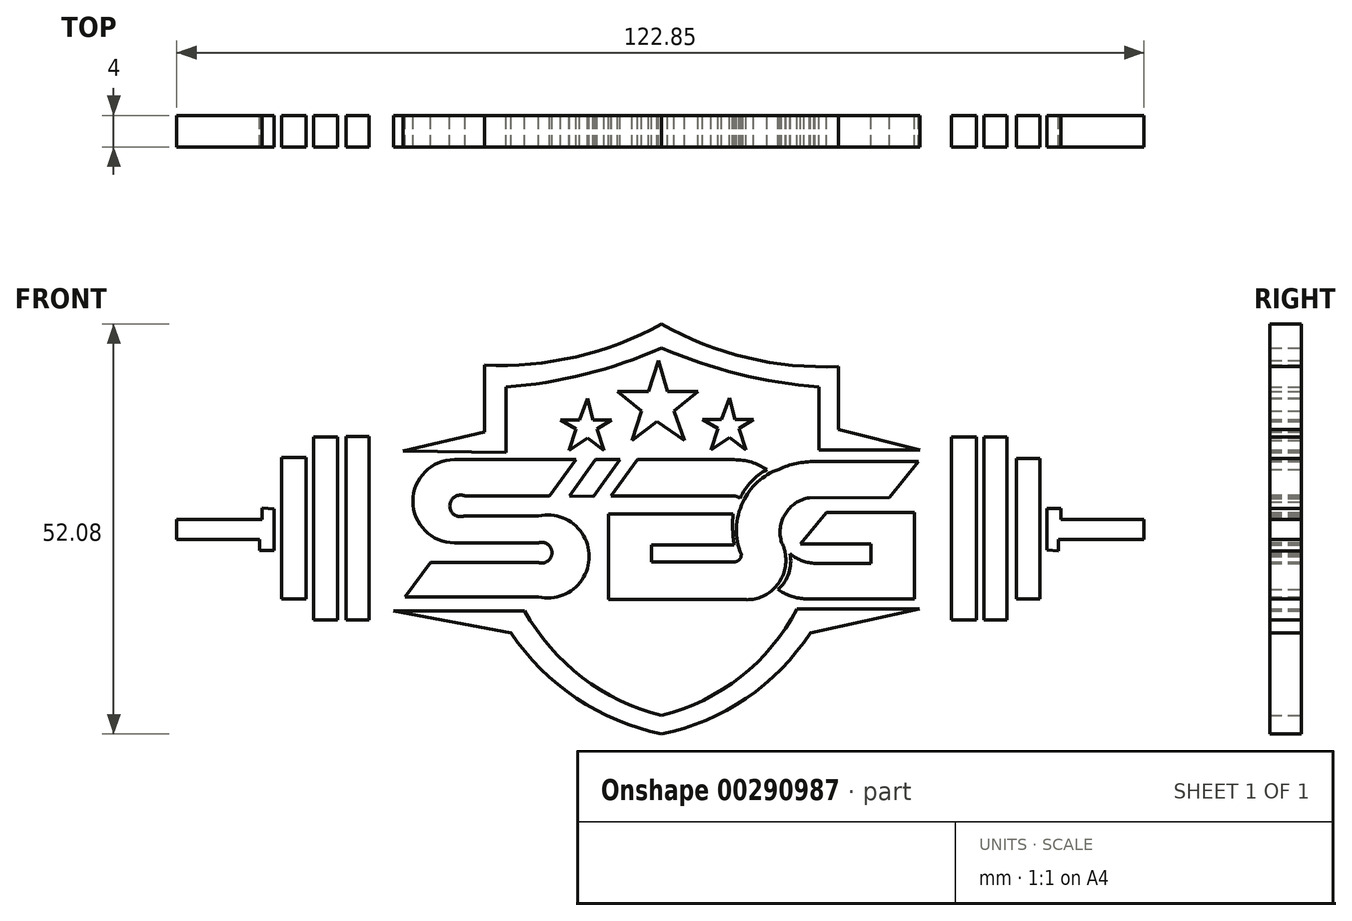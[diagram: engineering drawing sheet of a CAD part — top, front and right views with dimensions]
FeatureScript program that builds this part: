
annotation { "Feature Type Name" : "Feature", "Feature Type Description" : "" }
export const myFeature = defineFeature(function(context is Context, id is Id, definition is map)
    precondition{}
    {
        {
            var Q0;
            Q0=qCreatedBy(makeId("Front.planeOp"),FACE);
            var sketch = newSketch(context, id + "F0", { "sketchPlane" : qUnion([Q0])});
            skLineSegment(sketch, "E0", {"start": v(-28.73, 27.46) * mm, "end": v(-18.36, 29.84) * mm});
            skLineSegment(sketch, "E1", {"start": v(-18.36, 29.84) * mm, "end": v(-18.36, 38.37) * mm});
            skLineSegment(sketch, "E2", {"start": v(26.58, 38.16) * mm, "end": v(26.58, 30.16) * mm});
            skLineSegment(sketch, "E3", {"start": v(26.58, 30.16) * mm, "end": v(36.96, 27.57) * mm});
            skLineSegment(sketch, "E4", {"start": v(36.96, 27.57) * mm, "end": v(24.1, 27.57) * mm});
            skLineSegment(sketch, "E5", {"start": v(24.1, 27.57) * mm, "end": v(24.1, 35.56) * mm});
            skLineSegment(sketch, "E6", {"start": v(-15.66, 35.56) * mm, "end": v(-15.66, 27.24) * mm});
            skLineSegment(sketch, "E7", {"start": v(-15.66, 27.24) * mm, "end": v(-28.73, 27.46) * mm});
            skArc(sketch, "E8", {"start": v(-18.36, 38.37) * mm, "mid": v(-6.76, 39.4) * mm, "end": v(4.11, 43.56) * mm});
            skArc(sketch, "E9", {"start": v(4.11, 43.56) * mm, "mid": v(14.97, 39.29) * mm, "end": v(26.58, 38.16) * mm});
            skArc(sketch, "E10", {"start": v(-15.66, 35.56) * mm, "mid": v(-5.56, 37.2) * mm, "end": v(4.11, 40.53) * mm});
            skArc(sketch, "E11", {"start": v(4.11, 40.53) * mm, "mid": v(13.9, 37.21) * mm, "end": v(24.1, 35.56) * mm});
            skLineSegment(sketch, "E12", {"start": v(-29.92, 7.15) * mm, "end": v(-13.28, 7.15) * mm});
            skLineSegment(sketch, "E13", {"start": v(21.29, 7.37) * mm, "end": v(36.85, 7.37) * mm});
            skLineSegment(sketch, "E14", {"start": v(36.85, 7.37) * mm, "end": v(23.02, 4.34) * mm});
            skLineSegment(sketch, "E15", {"start": v(-15.01, 4.34) * mm, "end": v(-29.92, 7.15) * mm});
            skArc(sketch, "E16", {"start": v(-13.28, 7.15) * mm, "mid": v(-5.98, -1.32) * mm, "end": v(4.11, -6.14) * mm});
            skArc(sketch, "E17", {"start": v(4.11, -6.14) * mm, "mid": v(14.17, -1.26) * mm, "end": v(21.29, 7.37) * mm});
            skArc(sketch, "E18", {"start": v(4.11, -8.52) * mm, "mid": v(14.86, -4) * mm, "end": v(23.02, 4.34) * mm});
            skArc(sketch, "E19", {"start": v(-15.01, 4.34) * mm, "mid": v(-6.71, -3.97) * mm, "end": v(4.11, -8.52) * mm});
            skLineSegment(sketch, "E20.bottom", {"start": v(-35.97, 29.3) * mm, "end": v(-33.05, 29.3) * mm});
            skLineSegment(sketch, "E20.top", {"start": v(-35.97, 5.96) * mm, "end": v(-33.05, 5.96) * mm});
            skLineSegment(sketch, "E20.left", {"start": v(-35.97, 29.3) * mm, "end": v(-35.97, 5.96) * mm});
            skLineSegment(sketch, "E20.right", {"start": v(-33.05, 29.3) * mm, "end": v(-33.05, 5.96) * mm});
            skLineSegment(sketch, "E21.bottom", {"start": v(-40.08, 29.19) * mm, "end": v(-37.05, 29.19) * mm});
            skLineSegment(sketch, "E21.top", {"start": v(-40.08, 5.96) * mm, "end": v(-37.05, 5.96) * mm});
            skLineSegment(sketch, "E21.left", {"start": v(-40.08, 29.19) * mm, "end": v(-40.08, 5.96) * mm});
            skLineSegment(sketch, "E21.right", {"start": v(-37.05, 29.19) * mm, "end": v(-37.05, 5.96) * mm});
            skLineSegment(sketch, "E22.bottom", {"start": v(-44.18, 26.6) * mm, "end": v(-41.05, 26.6) * mm});
            skLineSegment(sketch, "E22.top", {"start": v(-44.18, 8.66) * mm, "end": v(-41.05, 8.66) * mm});
            skLineSegment(sketch, "E22.left", {"start": v(-44.18, 26.6) * mm, "end": v(-44.18, 8.66) * mm});
            skLineSegment(sketch, "E22.right", {"start": v(-41.05, 26.6) * mm, "end": v(-41.05, 8.66) * mm});
            skLineSegment(sketch, "E23.bottom", {"start": v(40.95, 29.19) * mm, "end": v(44.09, 29.19) * mm});
            skLineSegment(sketch, "E23.top", {"start": v(40.95, 5.96) * mm, "end": v(44.09, 5.96) * mm});
            skLineSegment(sketch, "E23.left", {"start": v(40.95, 29.19) * mm, "end": v(40.95, 5.96) * mm});
            skLineSegment(sketch, "E23.right", {"start": v(44.09, 29.19) * mm, "end": v(44.09, 5.96) * mm});
            skLineSegment(sketch, "E24.bottom", {"start": v(45.06, 29.19) * mm, "end": v(47.98, 29.19) * mm});
            skLineSegment(sketch, "E24.top", {"start": v(45.06, 5.96) * mm, "end": v(47.98, 5.96) * mm});
            skLineSegment(sketch, "E24.left", {"start": v(45.06, 29.19) * mm, "end": v(45.06, 5.96) * mm});
            skLineSegment(sketch, "E24.right", {"start": v(47.98, 29.19) * mm, "end": v(47.98, 5.96) * mm});
            skLineSegment(sketch, "E25.bottom", {"start": v(49.16, 26.49) * mm, "end": v(52.19, 26.49) * mm});
            skLineSegment(sketch, "E25.top", {"start": v(49.16, 8.66) * mm, "end": v(52.19, 8.66) * mm});
            skLineSegment(sketch, "E25.left", {"start": v(49.16, 26.49) * mm, "end": v(49.16, 8.66) * mm});
            skLineSegment(sketch, "E25.right", {"start": v(52.19, 26.49) * mm, "end": v(52.19, 8.66) * mm});
            skLineSegment(sketch, "E26", {"start": v(-45.11, 20.09) * mm, "end": v(-45.11, 14.82) * mm});
            skLineSegment(sketch, "E27", {"start": v(-45.11, 14.82) * mm, "end": v(-46.94, 14.82) * mm});
            skLineSegment(sketch, "E28", {"start": v(-46.94, 14.82) * mm, "end": v(-46.94, 16.2) * mm});
            skLineSegment(sketch, "E29", {"start": v(-46.94, 16.2) * mm, "end": v(-57.46, 16.2) * mm});
            skLineSegment(sketch, "E30", {"start": v(-57.46, 16.2) * mm, "end": v(-57.46, 18.72) * mm});
            skLineSegment(sketch, "E31", {"start": v(-57.46, 18.72) * mm, "end": v(-46.6, 18.72) * mm});
            skLineSegment(sketch, "E32", {"start": v(-46.6, 18.72) * mm, "end": v(-46.6, 20.2) * mm});
            skLineSegment(sketch, "E33", {"start": v(-46.6, 20.2) * mm, "end": v(-45.11, 20.09) * mm});
            skLineSegment(sketch, "E34", {"start": v(53.04, 14.85) * mm, "end": v(53.04, 20.12) * mm});
            skLineSegment(sketch, "E35", {"start": v(53.04, 20.12) * mm, "end": v(54.87, 20.12) * mm});
            skLineSegment(sketch, "E36", {"start": v(54.87, 20.12) * mm, "end": v(54.87, 18.74) * mm});
            skLineSegment(sketch, "E37", {"start": v(54.87, 18.74) * mm, "end": v(65.39, 18.74) * mm});
            skLineSegment(sketch, "E38", {"start": v(65.39, 18.74) * mm, "end": v(65.39, 16.22) * mm});
            skLineSegment(sketch, "E39", {"start": v(65.39, 16.22) * mm, "end": v(54.53, 16.22) * mm});
            skLineSegment(sketch, "E40", {"start": v(54.53, 16.22) * mm, "end": v(54.53, 14.74) * mm});
            skLineSegment(sketch, "E41", {"start": v(54.53, 14.74) * mm, "end": v(53.04, 14.85) * mm});
            skLineSegment(sketch, "E42", {"start": v(-8.71, 31.4) * mm, "end": v(-6.3, 31.4) * mm});
            skPoint(sketch, "E42.startSnap0", {"position": v(-15.66, 31.4) * mm});
            skLineSegment(sketch, "E43", {"start": v(-6.3, 31.4) * mm, "end": v(-5.28, 34.1) * mm});
            skLineSegment(sketch, "E44", {"start": v(-5.28, 34.1) * mm, "end": v(-4.56, 31.4) * mm});
            skLineSegment(sketch, "E45", {"start": v(-4.56, 31.4) * mm, "end": v(-2.22, 31.4) * mm});
            skLineSegment(sketch, "E46", {"start": v(-2.22, 31.4) * mm, "end": v(-4.06, 30.22) * mm});
            skLineSegment(sketch, "E47", {"start": v(-4.06, 30.22) * mm, "end": v(-3.2, 27.48) * mm});
            skLineSegment(sketch, "E48", {"start": v(-3.2, 27.48) * mm, "end": v(-5.28, 29.07) * mm});
            skLineSegment(sketch, "E49", {"start": v(-5.28, 29.07) * mm, "end": v(-7.63, 27.48) * mm});
            skLineSegment(sketch, "E50", {"start": v(-7.63, 27.48) * mm, "end": v(-6.76, 30.22) * mm});
            skLineSegment(sketch, "E51", {"start": v(-6.76, 30.22) * mm, "end": v(-8.71, 31.4) * mm});
            skLineSegment(sketch, "E52", {"start": v(3.55, 31.2) * mm, "end": v(0.34, 28.75) * mm});
            skLineSegment(sketch, "E53", {"start": v(0.34, 28.75) * mm, "end": v(1.57, 32.53) * mm});
            skLineSegment(sketch, "E54", {"start": v(1.57, 32.53) * mm, "end": v(-1.5, 34.99) * mm});
            skLineSegment(sketch, "E55", {"start": v(-1.5, 34.99) * mm, "end": v(2.47, 34.99) * mm});
            skLineSegment(sketch, "E56", {"start": v(2.47, 34.99) * mm, "end": v(3.75, 38.94) * mm});
            skLineSegment(sketch, "E57", {"start": v(3.75, 38.94) * mm, "end": v(4.85, 34.99) * mm});
            skLineSegment(sketch, "E58", {"start": v(4.85, 34.99) * mm, "end": v(8.75, 34.99) * mm});
            skLineSegment(sketch, "E59", {"start": v(8.75, 34.99) * mm, "end": v(5.72, 32.53) * mm});
            skLineSegment(sketch, "E60", {"start": v(5.72, 32.53) * mm, "end": v(7.02, 28.78) * mm});
            skLineSegment(sketch, "E61", {"start": v(7.02, 28.78) * mm, "end": v(3.55, 31.2) * mm});
            skLineSegment(sketch, "E62", {"start": v(9.32, 31.47) * mm, "end": v(11.72, 31.47) * mm});
            skLineSegment(sketch, "E63", {"start": v(11.72, 31.47) * mm, "end": v(12.75, 34.16) * mm});
            skLineSegment(sketch, "E64", {"start": v(12.75, 34.16) * mm, "end": v(13.46, 31.47) * mm});
            skLineSegment(sketch, "E65", {"start": v(13.46, 31.47) * mm, "end": v(15.8, 31.47) * mm});
            skLineSegment(sketch, "E66", {"start": v(15.8, 31.47) * mm, "end": v(13.97, 30.29) * mm});
            skLineSegment(sketch, "E67", {"start": v(13.97, 30.29) * mm, "end": v(14.83, 27.55) * mm});
            skLineSegment(sketch, "E68", {"start": v(14.83, 27.55) * mm, "end": v(12.75, 29.13) * mm});
            skLineSegment(sketch, "E69", {"start": v(12.75, 29.13) * mm, "end": v(10.4, 27.55) * mm});
            skLineSegment(sketch, "E70", {"start": v(10.4, 27.55) * mm, "end": v(11.27, 30.29) * mm});
            skLineSegment(sketch, "E71", {"start": v(11.27, 30.29) * mm, "end": v(9.32, 31.47) * mm});
            skLineSegment(sketch, "E72", {"start": v(-6.76, 26.33) * mm, "end": v(-22.2, 26.33) * mm});
            skPoint(sketch, "E72.endSnap0", {"position": v(-22.2, 27.35) * mm});
            skArc(sketch, "E73", {"start": v(-22.2, 26.33) * mm, "mid": v(-27.47, 21.05) * mm, "end": v(-22.2, 15.78) * mm});
            skLineSegment(sketch, "E74", {"start": v(-22.2, 15.78) * mm, "end": v(-11.5, 15.78) * mm});
            skLineSegment(sketch, "E75", {"start": v(-11.5, 13.26) * mm, "end": v(-25.22, 13.26) * mm});
            skLineSegment(sketch, "E76", {"start": v(-25.22, 13.26) * mm, "end": v(-28.48, 8.87) * mm});
            skLineSegment(sketch, "E77", {"start": v(-28.48, 8.87) * mm, "end": v(-11.5, 8.87) * mm});
            skLineSegment(sketch, "E78", {"start": v(-11.5, 19.2) * mm, "end": v(-20.87, 19.2) * mm});
            skLineSegment(sketch, "E79", {"start": v(-20.87, 21.72) * mm, "end": v(-10.1, 21.72) * mm});
            skLineSegment(sketch, "E80", {"start": v(-10.1, 21.72) * mm, "end": v(-6.76, 26.33) * mm});
            skArc(sketch, "E81", {"start": v(-20.87, 21.72) * mm, "mid": v(-22.78, 20.46) * mm, "end": v(-20.87, 19.2) * mm});
            skArc(sketch, "E82", {"start": v(-11.5, 13.26) * mm, "mid": v(-9.8, 14.52) * mm, "end": v(-11.5, 15.78) * mm});
            skArc(sketch, "E83", {"start": v(-11.5, 8.87) * mm, "mid": v(-5.1, 14.04) * mm, "end": v(-11.5, 19.2) * mm});
            skLineSegment(sketch, "E84", {"start": v(-4.24, 26.33) * mm, "end": v(-7.59, 21.72) * mm});
            skLineSegment(sketch, "E85", {"start": v(-7.59, 21.72) * mm, "end": v(-4.52, 21.67) * mm});
            skLineSegment(sketch, "E86", {"start": v(-4.52, 21.67) * mm, "end": v(-1.14, 26.33) * mm});
            skLineSegment(sketch, "E87", {"start": v(-1.14, 26.33) * mm, "end": v(-4.24, 26.33) * mm});
            skLineSegment(sketch, "E88", {"start": v(1.04, 26.33) * mm, "end": v(-2.3, 21.72) * mm});
            skLineSegment(sketch, "E89", {"start": v(-2.3, 21.72) * mm, "end": v(13.27, 21.72) * mm});
            skLineSegment(sketch, "E90", {"start": v(13.34, 26.33) * mm, "end": v(1.04, 26.33) * mm});
            skArc(sketch, "E91", {"start": v(17.5, 25.08) * mm, "mid": v(15.5, 26) * mm, "end": v(13.34, 26.33) * mm});
            skArc(sketch, "E92", {"start": v(17.5, 25.08) * mm, "mid": v(15.5, 23.52) * mm, "end": v(14.07, 21.43) * mm});
            skArc(sketch, "E93", {"start": v(14.07, 21.43) * mm, "mid": v(13.7, 21.65) * mm, "end": v(13.27, 21.72) * mm});
            skLineSegment(sketch, "E94", {"start": v(13.2, 19.4) * mm, "end": v(-2.62, 19.42) * mm});
            skLineSegment(sketch, "E95", {"start": v(-2.62, 19.42) * mm, "end": v(-2.62, 8.55) * mm});
            skLineSegment(sketch, "E96", {"start": v(-2.62, 8.55) * mm, "end": v(14.93, 8.55) * mm});
            skArc(sketch, "E97", {"start": v(14.93, 8.55) * mm, "mid": v(18.63, 10.2) * mm, "end": v(19.88, 14.06) * mm});
            skArc(sketch, "E98", {"start": v(19.88, 14.06) * mm, "mid": v(19.71, 14.96) * mm, "end": v(19.37, 15.8) * mm});
            skArc(sketch, "E99", {"start": v(22.88, 21.5) * mm, "mid": v(19.83, 19.45) * mm, "end": v(19.37, 15.8) * mm});
            skArc(sketch, "E100", {"start": v(13.2, 19.4) * mm, "mid": v(13.15, 17.46) * mm, "end": v(13.34, 15.52) * mm});
            skLineSegment(sketch, "E101", {"start": v(13.34, 15.52) * mm, "end": v(2.81, 15.53) * mm});
            skLineSegment(sketch, "E102", {"start": v(2.81, 15.53) * mm, "end": v(2.81, 13.36) * mm});
            skLineSegment(sketch, "E103", {"start": v(2.81, 13.36) * mm, "end": v(13.34, 13.35) * mm});
            skArc(sketch, "E104", {"start": v(13.34, 13.35) * mm, "mid": v(13.98, 13.62) * mm, "end": v(14.24, 14.27) * mm});
            skArc(sketch, "E105", {"start": v(14.47, 20.95) * mm, "mid": v(13.63, 17.64) * mm, "end": v(14.24, 14.27) * mm});
            skArc(sketch, "E106", {"start": v(19, 25.1) * mm, "mid": v(16.3, 23.5) * mm, "end": v(14.47, 20.95) * mm});
            skArc(sketch, "E107", {"start": v(23.6, 26.09) * mm, "mid": v(21.25, 25.86) * mm, "end": v(19, 25.1) * mm});
            skLineSegment(sketch, "E108", {"start": v(23.6, 26.09) * mm, "end": v(36.74, 26.09) * mm});
            skLineSegment(sketch, "E109", {"start": v(36.74, 26.09) * mm, "end": v(33.05, 21.53) * mm});
            skLineSegment(sketch, "E110", {"start": v(33.05, 21.53) * mm, "end": v(22.88, 21.5) * mm});
            skArc(sketch, "E111", {"start": v(18.92, 9.85) * mm, "mid": v(20.3, 11.94) * mm, "end": v(20.4, 14.44) * mm});
            skArc(sketch, "E112", {"start": v(18.92, 9.85) * mm, "mid": v(20.48, 9.02) * mm, "end": v(22.22, 8.67) * mm});
            skArc(sketch, "E113", {"start": v(20.4, 14.44) * mm, "mid": v(21.83, 13.56) * mm, "end": v(23.46, 13.17) * mm});
            skLineSegment(sketch, "E114", {"start": v(23.46, 13.17) * mm, "end": v(30.7, 13.17) * mm});
            skLineSegment(sketch, "E115", {"start": v(30.7, 13.17) * mm, "end": v(30.7, 15.64) * mm});
            skLineSegment(sketch, "E116", {"start": v(30.7, 15.64) * mm, "end": v(21.79, 15.64) * mm});
            skLineSegment(sketch, "E117", {"start": v(21.79, 15.64) * mm, "end": v(25.08, 19.6) * mm});
            skLineSegment(sketch, "E118", {"start": v(25.08, 19.6) * mm, "end": v(36.27, 19.6) * mm});
            skLineSegment(sketch, "E119", {"start": v(36.27, 19.6) * mm, "end": v(36.27, 8.67) * mm});
            skLineSegment(sketch, "E120", {"start": v(36.27, 8.67) * mm, "end": v(22.22, 8.67) * mm});
            skSolve(sketch);
        }
        {
            var Q0;
            Q0 = qSketchRegion(id + "F0", true);
            extrude(context, id + "F1", {"entities" : qUnion([Q0]), "depth" : 4 * mm});
        }
    });
